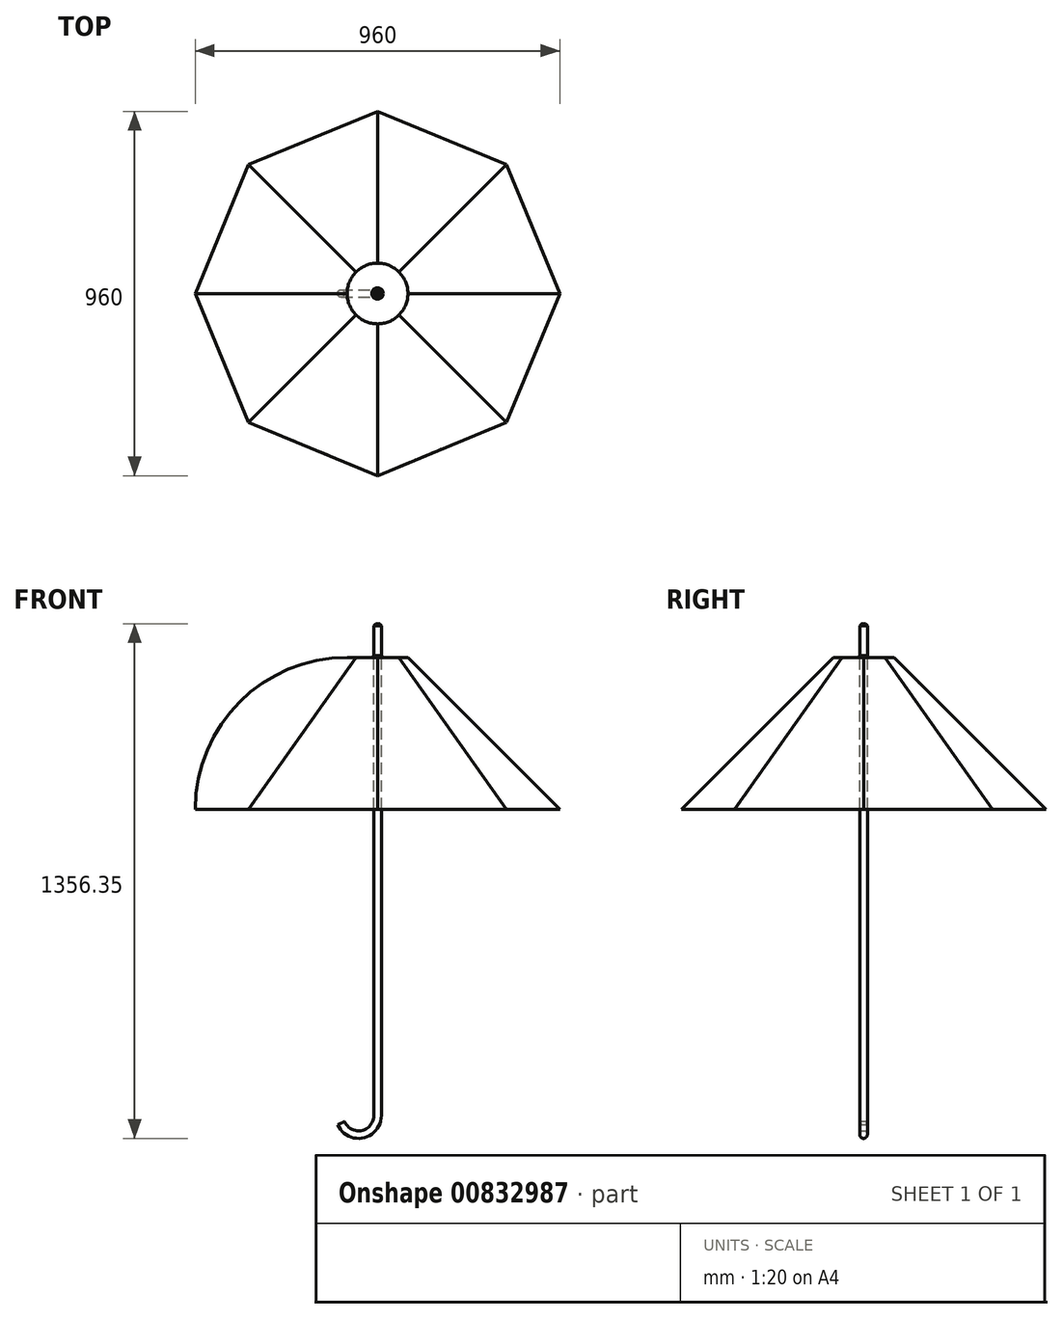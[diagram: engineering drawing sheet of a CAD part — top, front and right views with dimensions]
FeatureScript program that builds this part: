
annotation { "Feature Type Name" : "Feature", "Feature Type Description" : "" }
export const myFeature = defineFeature(function(context is Context, id is Id, definition is map)
    precondition{}
    {
        {
            var Q0;
            Q0=qCreatedBy(makeId("Top.planeOp"),FACE);
            cPlane(context, id + "F0", {"entities" : qUnion([Q0]), "cplaneType" : CPlaneType.OFFSET, "offset" : 400 * mm, "width" : 150 * mm, "height" : 150 * mm});
        }
        {
            var Q0;
            Q0=qCreatedBy(id+"F0.planeOp",FACE);
            var sketch = newSketch(context, id + "F1", { "sketchPlane" : qUnion([Q0])});
            skCircle(sketch, "E0", {"center": v(0, 0) * mm, "radius": 80 * mm});
            skSolve(sketch);
        }
        {
            var Q0;
            Q0=qCreatedBy(makeId("Top.planeOp"),FACE);
            var sketch = newSketch(context, id + "F2", { "sketchPlane" : qUnion([Q0])});
            skCircle(sketch, "E1.cCircle", {"center": v(0, 0) * mm, "radius": 443.46 * mm, "construction": true});
            skLineSegment(sketch, "E1.0", {"start": v(-339.41, -339.41) * mm, "end": v(-480, 0) * mm});
            skLineSegment(sketch, "E1.1", {"start": v(-480, 0) * mm, "end": v(-339.41, 339.41) * mm});
            skLineSegment(sketch, "E1.2", {"start": v(-339.41, 339.41) * mm, "end": v(0, 480) * mm});
            skLineSegment(sketch, "E1.3", {"start": v(0, 480) * mm, "end": v(339.41, 339.41) * mm});
            skLineSegment(sketch, "E1.4", {"start": v(339.41, 339.41) * mm, "end": v(480, 0) * mm});
            skLineSegment(sketch, "E1.5", {"start": v(480, 0) * mm, "end": v(339.41, -339.41) * mm});
            skLineSegment(sketch, "E1.6", {"start": v(339.41, -339.41) * mm, "end": v(0, -480) * mm});
            skLineSegment(sketch, "E1.7", {"start": v(0, -480) * mm, "end": v(-339.41, -339.41) * mm});
            skPoint(sketch, "E1.0.midPoint", {"position": v(-409.7, -169.7) * mm});
            skSolve(sketch);
        }
        {
            var Q0;
            Q0=qCreatedBy(makeId("Front.planeOp"),FACE);
            var sketch = newSketch(context, id + "F3", { "sketchPlane" : qUnion([Q0])});
            skArc(sketch, "E2", {"start": v(-80, 400) * mm, "mid": v(-362.84, 282.84) * mm, "end": v(-480, 0) * mm});
            skLineSegment(sketch, "E3", {"start": v(0, 0) * mm, "end": v(-80, 0) * mm});
            skSolve(sketch);
        }
        {
            var Q0;
            Q0=makeQuery(id+"F1.imprint","IMPRINT",FACE,{"disambiguationData":[TD([[makeQuery(id+"F1.imprint","IMPRINT",EDGE,{"derivedFrom":sQuery(id+"F1.wireOp",EDGE,"E0")}),1.0]])]});
            var Q1;
            Q1=makeQuery(id+"F2.imprint","IMPRINT",FACE,{"disambiguationData":[TD([[makeQuery(id+"F2.imprint","IMPRINT",EDGE,{"derivedFrom":sQuery(id+"F2.wireOp",EDGE,"E1.0")}),-1.0]])]});
            var Q2;
            Q2=sQuery(id+"F3.wireOp",EDGE,"E2");
            var Q3;
            Q3=sQuery(id+"FTbnOsWGeVRaXot_0.7.F3.wireOp",EDGE,"E2");
            var Q4;
            Q4=sQuery(id+"FTbnOsWGeVRaXot_0.6.F3.wireOp",EDGE,"E2");
            var Q5;
            Q5=sQuery(id+"FTbnOsWGeVRaXot_0.5.F3.wireOp",EDGE,"E2");
            var Q6;
            Q6=sQuery(id+"FTbnOsWGeVRaXot_0.4.F3.wireOp",EDGE,"E2");
            var Q7;
            Q7=sQuery(id+"FTbnOsWGeVRaXot_0.2.F3.wireOp",EDGE,"E2");
            var Q8;
            Q8=sQuery(id+"FTbnOsWGeVRaXot_0.1.F3.wireOp",EDGE,"E2");
            var Q9;
            Q9=sQuery(id+"FTbnOsWGeVRaXot_0.3.F3.wireOp",EDGE,"E2");
            loft(context, id + "F4", {"addGuides" : true, "sheetProfilesArray" : [{ "sheetProfileEntities" : qUnion([Q0]) }, { "sheetProfileEntities" : qUnion([Q1]) }], "guidesArray" : [{ "guideEntities" : qUnion([Q2]), "guideDerivativeType" : LoftGuideDerivativeType.DEFAULT, "guideDerivativeMagnitude" : 1 }, { "guideEntities" : qUnion([Q3]), "guideDerivativeType" : LoftGuideDerivativeType.DEFAULT, "guideDerivativeMagnitude" : 1 }, { "guideEntities" : qUnion([Q4]), "guideDerivativeType" : LoftGuideDerivativeType.DEFAULT, "guideDerivativeMagnitude" : 1 }, { "guideEntities" : qUnion([Q5]), "guideDerivativeType" : LoftGuideDerivativeType.DEFAULT, "guideDerivativeMagnitude" : 1 }, { "guideEntities" : qUnion([Q6]), "guideDerivativeType" : LoftGuideDerivativeType.DEFAULT, "guideDerivativeMagnitude" : 1 }, { "guideEntities" : qUnion([Q7]), "guideDerivativeType" : LoftGuideDerivativeType.DEFAULT, "guideDerivativeMagnitude" : 1 }, { "guideEntities" : qUnion([Q8]), "guideDerivativeType" : LoftGuideDerivativeType.DEFAULT, "guideDerivativeMagnitude" : 1 }, { "guideEntities" : qUnion([Q9]), "guideDerivativeType" : LoftGuideDerivativeType.DEFAULT, "guideDerivativeMagnitude" : 1 }]});
        }
        {
            var Q0;
            Q0=makeQuery(id+"F4.opLoft","CAP_FACE",FACE,{"disambiguationData":[OSD([makeQuery(id+"F2.imprint","IMPRINT",FACE,{"disambiguationData":[TD([[makeQuery(id+"F2.imprint","IMPRINT",EDGE,{"derivedFrom":sQuery(id+"F2.wireOp",EDGE,"E1.0")}),-1.0]])]})])],"isStart":true});
            shell(context, id + "F5", {"entities" : qUnion([Q0]), "thickness" : 1 * mm});
        }
        {
            var Q0;
            Q0=qCreatedBy(makeId("Front.planeOp"),FACE);
            var sketch = newSketch(context, id + "F6", { "sketchPlane" : qUnion([Q0])});
            skLineSegment(sketch, "E4", {"start": v(0, 488.85) * mm, "end": v(0, -807.5) * mm});
            skArc(sketch, "E5", {"start": v(-95.94, -827.23) * mm, "mid": v(-39.93, -856.48) * mm, "end": v(0, -807.5) * mm});
            skLineSegment(sketch, "E6", {"start": v(0, -807.5) * mm, "end": v(0, -807.5) * mm});
            skSolve(sketch);
        }
        {
            var Q0;
            Q0=qCreatedBy(id+"F0.planeOp",FACE);
            var sketch = newSketch(context, id + "F7", { "sketchPlane" : qUnion([Q0])});
            skCircle(sketch, "E7", {"center": v(0, 0) * mm, "radius": 10 * mm});
            skSolve(sketch);
        }
        {
            var Q0;
            Q0 = qSketchRegion(id + "F7", true);
            var Q1;
            Q1=sQuery(id+"F6.wireOp",EDGE,"E4");
            var Q2;
            Q2=sQuery(id+"F6.wireOp",EDGE,"E5");
            sweep(context, id + "F8", {"operationType" : NewBodyOperationType.ADD, "profiles" : qUnion([Q0]), "path" : qUnion([Q1, Q2])});
        }
        {
            var Q0;
            {var subQ0=sQuery(id+"F7.wireOp",EDGE,"E7");Q0=makeQuery(id+"F8.boolean.opBoolean","SPLIT",FACE,{"disambiguationData":[TD([makeQuery(id+"F4.opLoft","CAP_FACE",FACE,{"disambiguationData":[OSD([makeQuery(id+"F1.imprint","IMPRINT",FACE,{"disambiguationData":[TD([[makeQuery(id+"F1.imprint","IMPRINT",EDGE,{"derivedFrom":sQuery(id+"F1.wireOp",EDGE,"E0")}),1.0]])]})])],"isStart":true})])],"derivedFrom":makeQuery(id+"F8.opSweep","SWEPT_FACE",FACE,{"disambiguationData":[OSD([sQuery(id+"F6.wireOp",EDGE,"E4"),subQ0])]})});}
            chamfer(context, id + "F9", {"entities" : qUnion([Q0]), "width" : 5 * mm, "tangentPropagation" : true});
        }
    });
